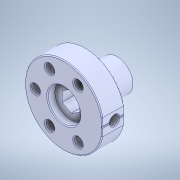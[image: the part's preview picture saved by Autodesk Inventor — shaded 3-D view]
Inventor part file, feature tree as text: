
AUTODESK INVENTOR PART (.ipt)
format: ipt  version: 2020.2 (Build 242310000, 310)  size: 206,848 bytes
history: native  units: in
note: dims shown in document units (in); Inventor stores cm internally (conversion verified against a paired STEP export)
features: fillet x1
ambient origin geometry x8: Origin, YZ Plane, XZ Plane, XY Plane, X Axis, Y Axis, Z Axis, Center Point
bodies: Solid1 (feature_tree)
feature tree (1):
  fillet  "Fillet2"  [1 undecoded]
note: 1 required parameter value undecoded (feature->parameter linkage not recoverable at this tier; creation-order binding heuristic only, values carry confidence <= 0.55)
